# Revit family: QF_COZIL_CZGCP-35N
name_source: partatom
category: Equipamento especial
units: mm (PartAtom-declared; Revit-internal decimal feet)

## family parameters
Com base no plano de trabalho = Não
Compartilhado = Não
Corte com vazios quando carregada = Não
Cota do conector redondo = Utilizar diâmetro
Número OmniClass = 23.40.40.14.17.24
Ponto de cálculo do ambiente = Não
Sempre na vertical = Sim
Tipo de parte = Normal
Título OmniClass = Fryers

## types (1)
- CZGCP-35N
    Capacity in Liters = 17 L
    Descrição = COZEDOR DE MASSAS MODULAR A GAS C/ RODIZIOS 5 POL - 350X743X940MM(COMPACT LINE II)
    Drain Connection Height = 251  [stored 0.823491 ft]
    Drain Size = 3/4"
    Elevação padrão = 0  [stored 0 ft]
    Fabricante = COZIL
    Gas Conenction Height = 295  [stored 0.967848 ft]
    Gas Consumption GLP = 0.536 kg/h
    Gas Consumption GN = 0.7 m³/h
    Gas Input GLP = 24444 Btu/h
    Gas Input GN = 6164 kcal/h
    Gas Pressure GLP = 0.3 bar
    Gas Pressure GN = 0.2 bar
    Gas Size = 1/2"
    Modelo = CZGCP-35N
    URL = https://cozil.com.br
    Water Connection Height = 295  [stored 0.967848 ft]
    Water Size = 3/4"

note: [stored X ft] marks values corroborated as IEEE doubles in the binary element streams (Revit-internal decimal feet)

## geometry (parser evidence)
native form markers: Sweep x3
no freeform markers — native parametric forms only
